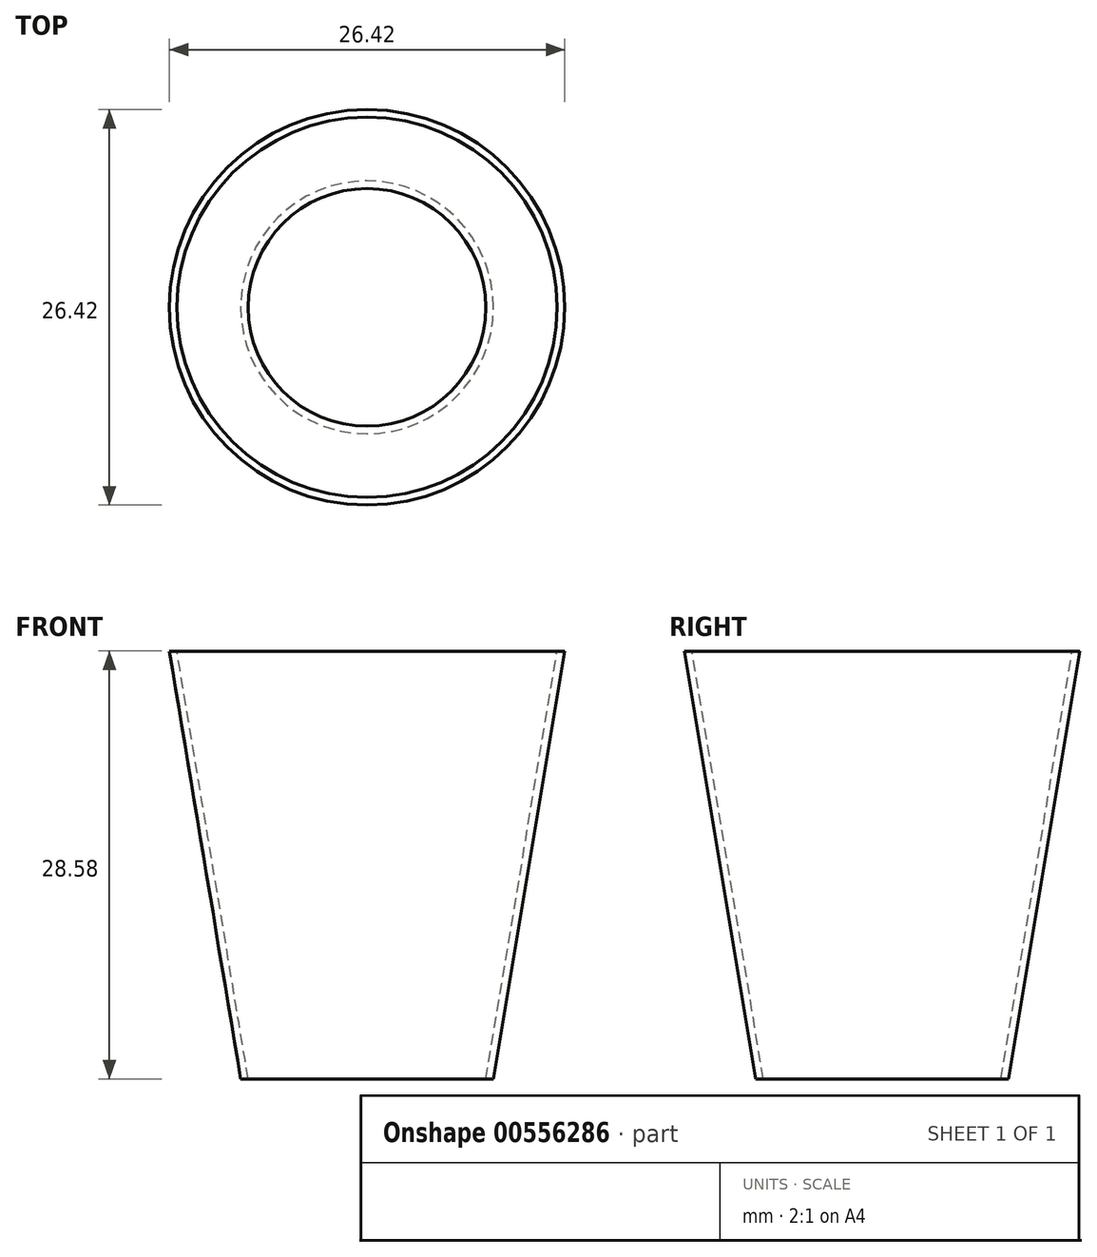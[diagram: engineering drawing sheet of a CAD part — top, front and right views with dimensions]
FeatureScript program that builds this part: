
annotation { "Feature Type Name" : "Feature", "Feature Type Description" : "" }
export const myFeature = defineFeature(function(context is Context, id is Id, definition is map)
    precondition{}
    {
        {
            var Q0;
            Q0=qCreatedBy(makeId("Front.planeOp"),FACE);
            var sketch = newSketch(context, id + "F0", { "sketchPlane" : qUnion([Q0])});
            skLineSegment(sketch, "E0", {"start": v(12.7, 28.58) * mm, "end": v(13.2, 28.58) * mm});
            skLineSegment(sketch, "E1", {"start": v(13.2, 28.58) * mm, "end": v(8.45, 0) * mm});
            skLineSegment(sketch, "E2", {"start": v(8.45, 0) * mm, "end": v(7.94, 0) * mm});
            skLineSegment(sketch, "E3", {"start": v(7.94, 0) * mm, "end": v(12.7, 28.58) * mm});
            skLineSegment(sketch, "E4", {"start": v(0, 0) * mm, "end": v(0, 28.58) * mm, "construction": true});
            skSolve(sketch);
        }
        {
            var Q0;
            Q0=makeQuery(id+"F0.imprint","IMPRINT",FACE,{"disambiguationData":[TD([[makeQuery(id+"F0.imprint","IMPRINT",EDGE,{"derivedFrom":sQuery(id+"F0.wireOp",EDGE,"E0")}),-1.0]])]});
            var Q1;
            Q1=sQuery(id+"F0.wireOp",EDGE,"E4");
            revolve(context, id + "F1", {"entities" : qUnion([Q0]), "axis" : qUnion([Q1]), "revolveType" : RevolveType.FULL});
        }
    });
